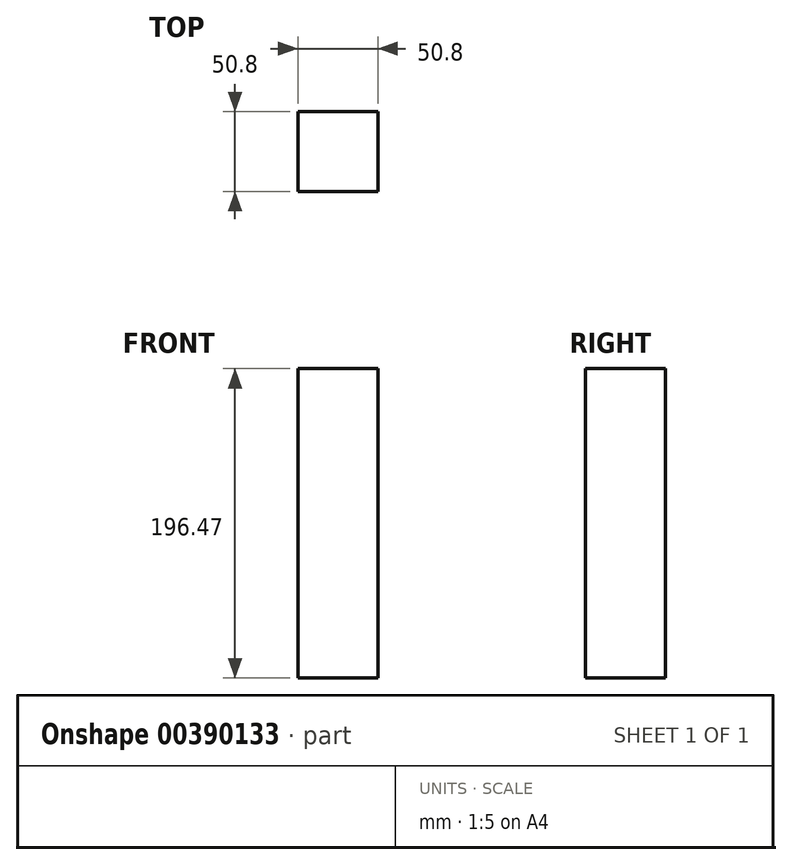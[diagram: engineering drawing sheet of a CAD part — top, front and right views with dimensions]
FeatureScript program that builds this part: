
annotation { "Feature Type Name" : "Feature", "Feature Type Description" : "" }
export const myFeature = defineFeature(function(context is Context, id is Id, definition is map)
    precondition{}
    {
        {
            var Q0;
            Q0=qCreatedBy(makeId("Top.planeOp"),FACE);
            var sketch = newSketch(context, id + "F0", { "sketchPlane" : qUnion([Q0])});
            skLineSegment(sketch, "E0.bottom", {"start": v(0, 0) * mm, "end": v(50.8, 0) * mm});
            skLineSegment(sketch, "E0.top", {"start": v(0, 50.8) * mm, "end": v(50.8, 50.8) * mm});
            skLineSegment(sketch, "E0.left", {"start": v(0, 0) * mm, "end": v(0, 50.8) * mm});
            skLineSegment(sketch, "E0.right", {"start": v(50.8, 0) * mm, "end": v(50.8, 50.8) * mm});
            skSolve(sketch);
        }
        {
            var Q0;
            Q0=makeQuery(id+"F0.imprint","IMPRINT",FACE,{"disambiguationData":[TD([[makeQuery(id+"F0.imprint","IMPRINT",EDGE,{"derivedFrom":sQuery(id+"F0.wireOp",EDGE,"E0.bottom")}),1.0]])]});
            extrude(context, id + "F1", {"entities" : qUnion([Q0]), "depth" : 196.47 * mm});
        }
    });
